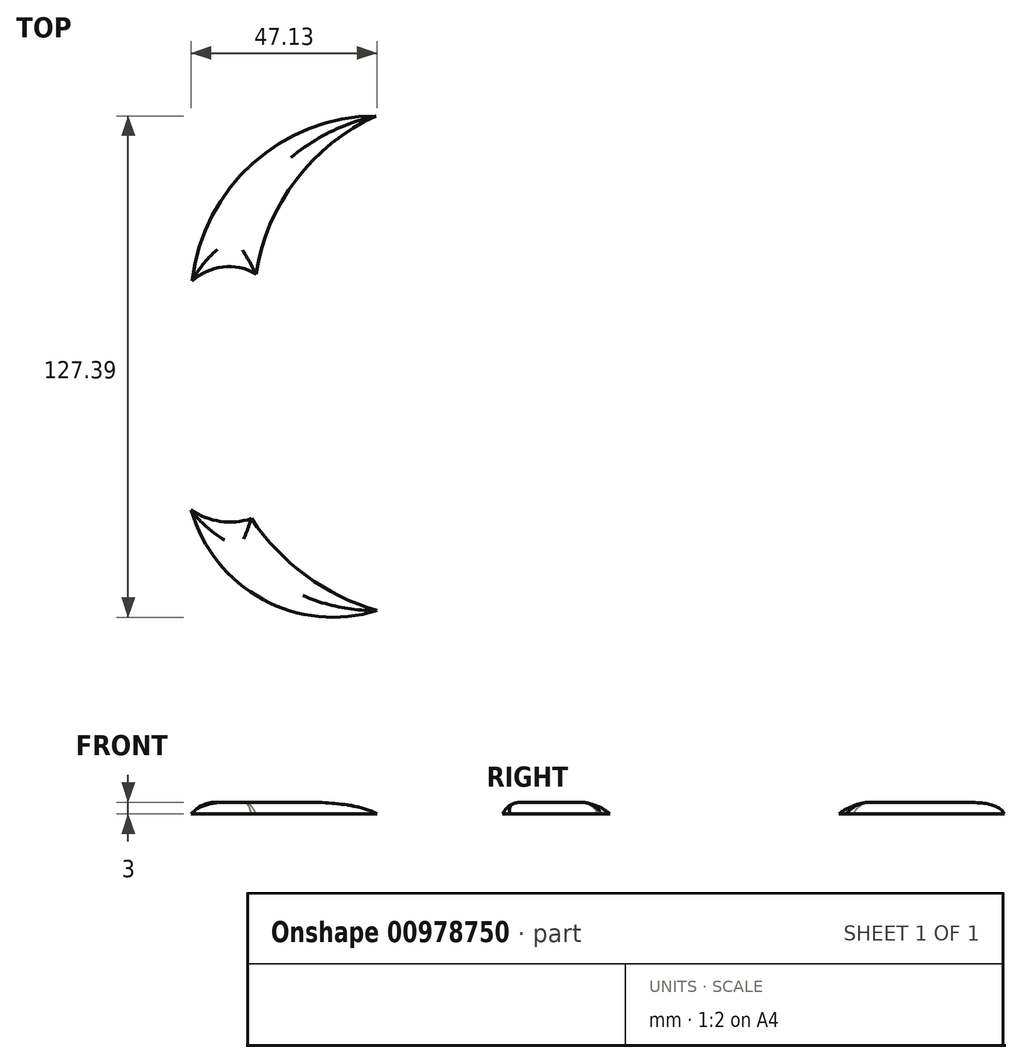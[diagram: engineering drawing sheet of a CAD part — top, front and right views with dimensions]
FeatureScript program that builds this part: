
annotation { "Feature Type Name" : "Feature", "Feature Type Description" : "" }
export const myFeature = defineFeature(function(context is Context, id is Id, definition is map)
    precondition{}
    {
        {
            var Q0;
            Q0=qCreatedBy(makeId("Top.planeOp"),FACE);
            var sketch = newSketch(context, id + "F0", { "sketchPlane" : qUnion([Q0])});
            skLineSegment(sketch, "E0", {"start": v(-59.18, 0) * mm, "end": v(66.72, 0) * mm, "construction": true});
            skLineSegment(sketch, "E1", {"start": v(-46.61, 0) * mm, "end": v(-46.61, 12.45) * mm, "construction": true});
            skLineSegment(sketch, "E2", {"start": v(-12.9, 32.6) * mm, "end": v(36.23, 24.26) * mm});
            skLineSegment(sketch, "E3", {"start": v(-12.9, 32.6) * mm, "end": v(-46.61, 12.45) * mm});
            skArc(sketch, "E4", {"start": v(-46.61, 12.45) * mm, "mid": v(-53.65, 6.99) * mm, "end": v(-59.18, 0) * mm});
            skArc(sketch, "E5", {"start": v(-4.94, 59.6) * mm, "mid": v(-14.8, 46.44) * mm, "end": v(-17.01, 30.14) * mm});
            skArc(sketch, "E6", {"start": v(-4.94, 59.6) * mm, "mid": v(-8.02, 45.88) * mm, "end": v(-8.47, 31.84) * mm});
            skLineSegment(sketch, "E7", {"start": v(36.23, 24.26) * mm, "end": v(67.25, 6.57) * mm});
            skSolve(sketch);
        }
        {
            var Q0;
            Q0=sQuery(id+"F0.wireOp",EDGE,"E2");
            var Q1;
            Q1=sQuery(id+"F0.wireOp",EDGE,"E7");
            var Q2;
            Q2=sQuery(id+"F0.wireOp",EDGE,"E3");
            var Q3;
            Q3=sQuery(id+"F0.wireOp",EDGE,"E4");
            var Q4;
            Q4=sQuery(id+"F0.wireOp",EDGE,"E0");
            revolve(context, id + "F1", {"bodyType" : ToolBodyType.SURFACE, "surfaceOperationType" : NewSurfaceOperationType.NEW, "surfaceEntities" : qUnion([Q0, Q1, Q2, Q3]), "axis" : qUnion([Q4]), "revolveType" : RevolveType.FULL});
        }
        {
            var Q0;
            Q0=makeQuery(id+"F1.opRevolve","SWEPT_EDGE",EDGE,{"disambiguationData":[OSD([sQuery(id+"F0.wireOp",VERTEX,"E3.start")])]});
            var Q1;
            Q1=makeQuery(id+"F1.opRevolve","SWEPT_EDGE",EDGE,{"disambiguationData":[OSD([sQuery(id+"F0.wireOp",VERTEX,"E7.start")])]});
            var Q2;
            Q2=makeQuery(id+"F1.opRevolve","SWEPT_EDGE",EDGE,{"disambiguationData":[OSD([sQuery(id+"F0.wireOp",VERTEX,"E4.start")])]});
            fillet(context, id + "F2", {"entities" : qUnion([Q0, Q1, Q2]), "radius" : 20 * mm, "tangentPropagation" : true, "allowEdgeOverflow" : false});
        }
        {
            var Q0;
            Q0=qCreatedBy(makeId("Top.planeOp"),FACE);
            var sketch = newSketch(context, id + "F3", { "sketchPlane" : qUnion([Q0])});
            skArc(sketch, "E8", {"start": v(26.34, 71.06) * mm, "mid": v(-5, 58.96) * mm, "end": v(-20.34, 29.07) * mm});
            skArc(sketch, "E9", {"start": v(26.34, 71.06) * mm, "mid": v(6.05, 54.8) * mm, "end": v(-4.17, 30.9) * mm});
            skArc(sketch, "E10", {"start": v(-20.58, -29.06) * mm, "mid": v(-2.4, -51.79) * mm, "end": v(26.55, -54.66) * mm});
            skArc(sketch, "E11", {"start": v(-5.3, -31.27) * mm, "mid": v(8.57, -45.75) * mm, "end": v(26.55, -54.66) * mm});
            skArc(sketch, "E12", {"start": v(-4.17, 30.9) * mm, "mid": v(-12.56, 32.67) * mm, "end": v(-20.34, 29.07) * mm});
            skArc(sketch, "E13", {"start": v(-20.58, -29.06) * mm, "mid": v(-13.2, -31.96) * mm, "end": v(-5.3, -31.27) * mm});
            skSolve(sketch);
        }
        {
            var Q0;
            Q0=makeQuery(id+"F3.imprint","IMPRINT",FACE,{"disambiguationData":[TD([[makeQuery(id+"F3.imprint","IMPRINT",EDGE,{"derivedFrom":sQuery(id+"F3.wireOp",EDGE,"E10")}),1.0]])]});
            var Q1;
            Q1=makeQuery(id+"F3.imprint","IMPRINT",FACE,{"disambiguationData":[TD([[makeQuery(id+"F3.imprint","IMPRINT",EDGE,{"derivedFrom":sQuery(id+"F3.wireOp",EDGE,"E8")}),1.0]])]});
            extrude(context, id + "F4", {"entities" : qUnion([Q0, Q1]), "depth" : 3 * mm, "offsetDistance" : 25 * mm});
        }
        {
            var Q0;
            Q0=makeQuery(id+"F4.opExtrude","CAP_FACE",FACE,{"disambiguationData":[OSD([sQuery(id+"F3.wireOp",EDGE,"E8"),sQuery(id+"F3.wireOp",EDGE,"E9"),sQuery(id+"F3.wireOp",EDGE,"E12")])],"isStart":false});
            var Q1;
            Q1=makeQuery(id+"F4.opExtrude","CAP_FACE",FACE,{"disambiguationData":[OSD([sQuery(id+"F3.wireOp",EDGE,"E10"),sQuery(id+"F3.wireOp",EDGE,"E11"),sQuery(id+"F3.wireOp",EDGE,"E13")])],"isStart":false});
            fillet(context, id + "F5", {"entities" : qUnion([Q0, Q1]), "radius" : 5 * mm, "tangentPropagation" : true, "allowEdgeOverflow" : false});
        }
    });
